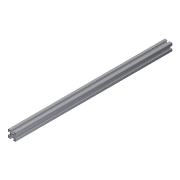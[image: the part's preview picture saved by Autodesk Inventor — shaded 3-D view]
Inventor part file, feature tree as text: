
AUTODESK INVENTOR PART (.ipt)
format: ipt  version: 2011 (Build 150239000, 239)  size: 311,808 bytes
history: native  units: in
note: dims shown in document units (in); Inventor stores cm internally (conversion verified against a paired STEP export)
features: plane x3, sketch x2, extrude x1, hole x1
ambient origin geometry x8: Origin, YZ Plane, XZ Plane, XY Plane, X Axis, Y Axis, Z Axis, Center Point
bodies: Solid1 (feature_tree)
feature tree (7):
  extrude  "Extrusion1"  TaperAngle=0.0deg  [1 undecoded]
  plane  "Work Plane2"
  plane  "Work Plane3"
  plane  "Work Plane4"
  hole  "Hole1"  [1 undecoded]
  sketch  "Sketch1"  dims[d0=15.9252in d1=0.0in d4=0.0in]
  sketch  "Sketch4"  dims[d5=0.0in d6=0.0in d7=0.9997in d8=0.3937in d9=15.9252in d10=7.9625in d11=0.9997in d12=0.3937in d13=0.25in d14=0.75in d15=0.375in d16=0.25in d17=0.5635in d18=1.0in d19=0.8108in]
note: 2 required parameter values undecoded (feature->parameter linkage not recoverable at this tier; creation-order binding heuristic only, values carry confidence <= 0.55)
